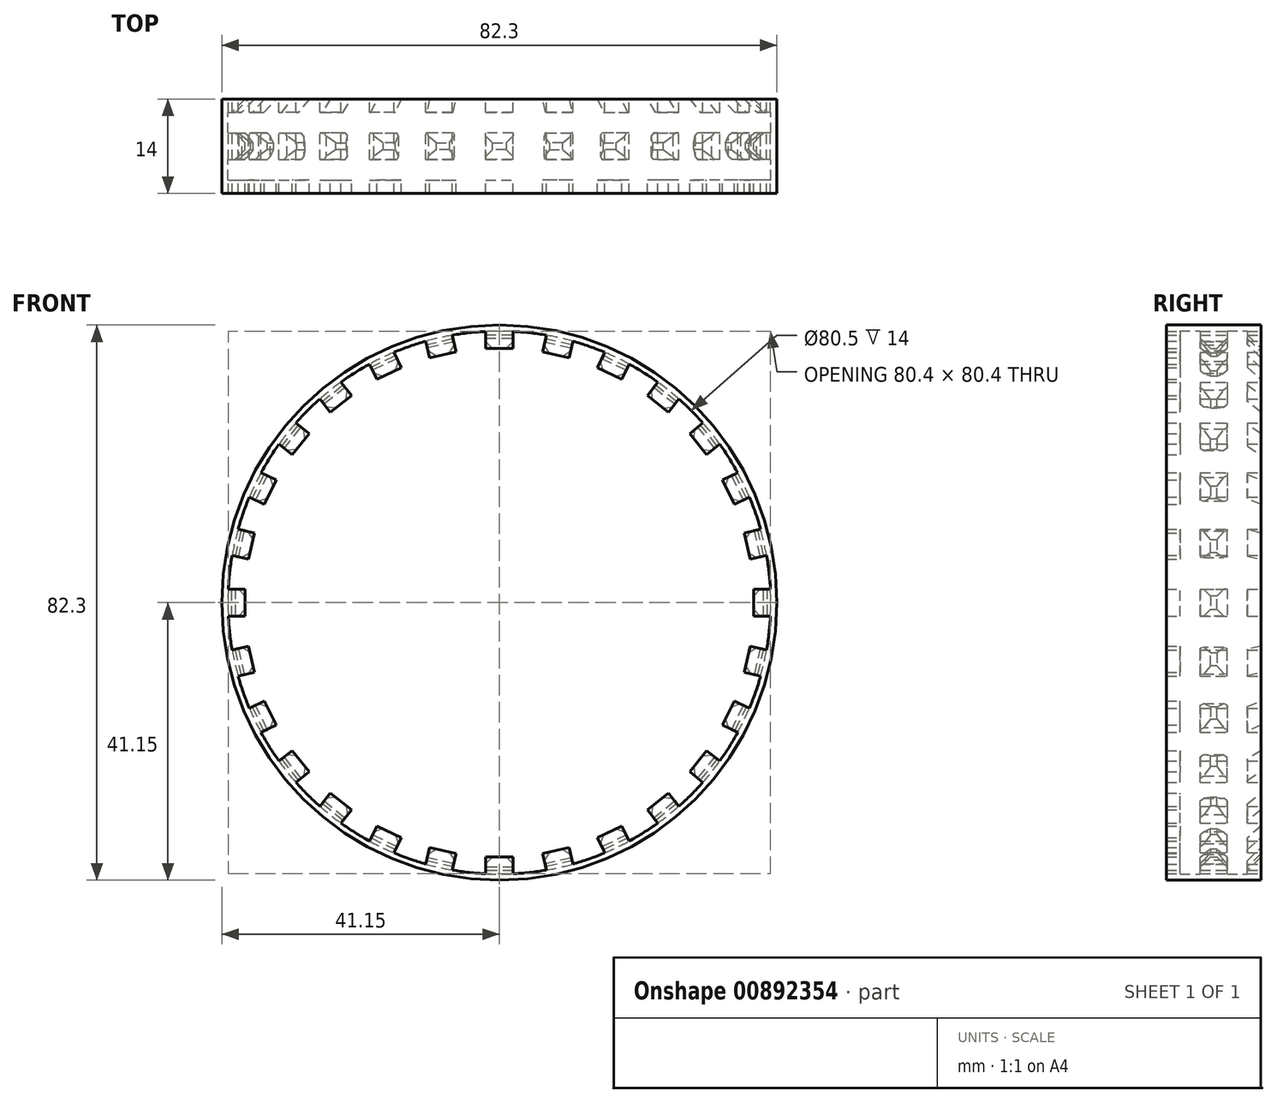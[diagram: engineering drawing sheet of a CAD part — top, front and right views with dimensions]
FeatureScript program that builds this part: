
annotation { "Feature Type Name" : "Feature", "Feature Type Description" : "" }
export const myFeature = defineFeature(function(context is Context, id is Id, definition is map)
    precondition{}
    {
        {
            var Q0;
            Q0=qCreatedBy(makeId("Top.planeOp"),FACE);
            var sketch = newSketch(context, id + "F0", { "sketchPlane" : qUnion([Q0])});
            skLineSegment(sketch, "E0", {"start": v(0, 44.68) * mm, "end": v(0, -51.28) * mm, "construction": true});
            skSolve(sketch);
        }
        {
            var Q0;
            Q0=qCreatedBy(makeId("Front.planeOp"),FACE);
            var sketch = newSketch(context, id + "F1", { "sketchPlane" : qUnion([Q0])});
            skCircle(sketch, "E1", {"center": v(0, 0) * mm, "radius": 40.25 * mm});
            skCircle(sketch, "E2", {"center": v(0, 0) * mm, "radius": 41.15 * mm});
            skLineSegment(sketch, "E3", {"start": v(0, 41.15) * mm, "end": v(0, 40.25) * mm, "construction": true});
            skPoint(sketch, "E4", {"position": v(0, 40.7) * mm});
            skCircle(sketch, "E5", {"center": v(0, 40.7) * mm, "radius": 2 * mm});
            skLineSegment(sketch, "E6.top", {"start": v(-2, 37.7) * mm, "end": v(2, 37.7) * mm});
            skLineSegment(sketch, "E6.left", {"start": v(-2, 40.2) * mm, "end": v(-2, 37.7) * mm});
            skLineSegment(sketch, "E6.right", {"start": v(2, 40.2) * mm, "end": v(2, 37.7) * mm});
            skPoint(sketch, "E7.orphan", {"position": v(2, 40.7) * mm});
            skPoint(sketch, "E8.orphan", {"position": v(-2, 40.7) * mm});
            skSolve(sketch);
        }
        {
            var Q0;
            {var subQ0=sQuery(id+"F1.wireOp",EDGE,"E1");var subQ2=makeQuery(id+"F1.imprint","INTERSECT",VERTEX,{"derivedFrom":[subQ0,sQuery(id+"F1.wireOp",EDGE,"E6.right")]});Q0=makeQuery(id+"F1.imprint","IMPRINT",FACE,{"disambiguationData":[TD([[makeQuery(id+"F1.imprint","IMPRINT",EDGE,{"disambiguationData":[TD([[subQ2,-1.0]])],"derivedFrom":subQ0}),-1.0]])]});}
            var Q1;
            {var subQ0=sQuery(id+"F1.wireOp",EDGE,"E5");var subQ1=sQuery(id+"F1.wireOp",EDGE,"E1");var subQ2=makeQuery(id+"F1.imprint","INTERSECT",VERTEX,{"disambiguationData":[OD(0.0)],"derivedFrom":[subQ1,subQ0]});Q1=makeQuery(id+"F1.imprint","IMPRINT",FACE,{"disambiguationData":[TD([[makeQuery(id+"F1.imprint","IMPRINT",EDGE,{"disambiguationData":[TD([[subQ2,-1.0]])],"derivedFrom":subQ1}),-1.0]])]});}
            extrude(context, id + "F2", {"entities" : qUnion([Q0, Q1]), "endBound" : BoundingType.SYMMETRIC, "depth" : 14 * mm, "offsetDistance" : 25 * mm});
        }
        {
            var Q0;
            {var subQ0=sQuery(id+"F1.wireOp",EDGE,"E5");var subQ1=sQuery(id+"F1.wireOp",EDGE,"E2");var subQ2=makeQuery(id+"F1.imprint","INTERSECT",VERTEX,{"disambiguationData":[OD(0.0)],"derivedFrom":[subQ1,subQ0]});Q0=makeQuery(id+"F1.imprint","IMPRINT",FACE,{"disambiguationData":[TD([[makeQuery(id+"F1.imprint","IMPRINT",EDGE,{"disambiguationData":[TD([[subQ2,1.0]])],"derivedFrom":subQ1}),-1.0]])]});}
            var Q1;
            {var subQ0=sQuery(id+"F1.wireOp",EDGE,"E5");var subQ1=sQuery(id+"F1.wireOp",EDGE,"E1");var subQ2=makeQuery(id+"F1.imprint","INTERSECT",VERTEX,{"disambiguationData":[OD(0.0)],"derivedFrom":[subQ1,subQ0]});Q1=makeQuery(id+"F1.imprint","IMPRINT",FACE,{"disambiguationData":[TD([[makeQuery(id+"F1.imprint","IMPRINT",EDGE,{"disambiguationData":[TD([[subQ2,-1.0]])],"derivedFrom":subQ1}),1.0]])]});}
            var Q2;
            {var subQ0=sQuery(id+"F1.wireOp",EDGE,"E6.right");Q2=makeQuery(id+"F1.imprint","IMPRINT",FACE,{"disambiguationData":[TD([[makeQuery(id+"F1.imprint","IMPRINT",EDGE,{"derivedFrom":subQ0}),-1.0]])]});}
            var Q3;
            {var subQ0=sQuery(id+"F1.wireOp",EDGE,"E6.left");Q3=makeQuery(id+"F1.imprint","IMPRINT",FACE,{"disambiguationData":[TD([[makeQuery(id+"F1.imprint","IMPRINT",EDGE,{"derivedFrom":subQ0}),1.0]])]});}
            var Q4;
            Q4=sQuery(id+"F1.wireOp",EDGE,"E5");
            extrude(context, id + "F3", {"entities" : qUnion([Q0, Q1, Q2, Q3]), "surfaceEntities" : qUnion([Q4]), "endBound" : BoundingType.SYMMETRIC, "depth" : 14 * mm, "offsetDistance" : 25 * mm});
        }
        {
            var Q0;
            {var subQ0=sQuery(id+"F1.wireOp",EDGE,"E5");var subQ1=sQuery(id+"F1.wireOp",EDGE,"E1");var subQ2=makeQuery(id+"F1.imprint","INTERSECT",VERTEX,{"disambiguationData":[OD(0.0)],"derivedFrom":[subQ1,subQ0]});Q0=makeQuery(id+"F1.imprint","IMPRINT",FACE,{"disambiguationData":[TD([[makeQuery(id+"F1.imprint","IMPRINT",EDGE,{"disambiguationData":[TD([[subQ2,1.0]])],"derivedFrom":subQ1}),1.0]])]});}
            var Q1;
            {var subQ0=sQuery(id+"F1.wireOp",EDGE,"E5");var subQ1=sQuery(id+"F1.wireOp",EDGE,"E1");var subQ2=makeQuery(id+"F1.imprint","INTERSECT",VERTEX,{"disambiguationData":[OD(0.0)],"derivedFrom":[subQ1,subQ0]});Q1=makeQuery(id+"F1.imprint","IMPRINT",FACE,{"disambiguationData":[TD([[makeQuery(id+"F1.imprint","IMPRINT",EDGE,{"disambiguationData":[TD([[subQ2,-1.0]])],"derivedFrom":subQ1}),1.0]])]});}
            var Q2;
            {var subQ0=sQuery(id+"F1.wireOp",EDGE,"E6.left");var subQ1=sQuery(id+"F1.wireOp",EDGE,"E1");var subQ2=makeQuery(id+"F1.imprint","INTERSECT",VERTEX,{"derivedFrom":[subQ1,subQ0]});Q2=makeQuery(id+"F1.imprint","IMPRINT",FACE,{"disambiguationData":[TD([[makeQuery(id+"F1.imprint","IMPRINT",EDGE,{"disambiguationData":[TD([[subQ2,1.0]])],"derivedFrom":subQ1}),1.0]])]});}
            var Q3;
            Q3=sQuery(id+"F1.wireOp",EDGE,"E5");
            extrude(context, id + "F4", {"entities" : qUnion([Q0, Q1, Q2]), "operationType" : NewBodyOperationType.REMOVE, "surfaceEntities" : qUnion([Q3]), "endBound" : BoundingType.SYMMETRIC, "oppositeDirection" : true, "depth" : 10 * mm, "offsetDistance" : 25 * mm});
        }
        {
            var Q0;
            Q0=makeQuery(id+"F4.boolean.opBoolean","COPY",EDGE,{"derivedFrom":makeQuery(id+"F4.opExtrude","CAP_EDGE",EDGE,{"disambiguationData":[OSD([sQuery(id+"F1.wireOp",EDGE,"E6.top")])],"isStart":false})});
            var Q1;
            Q1=makeQuery(id+"F4.boolean.opBoolean","COPY",EDGE,{"derivedFrom":makeQuery(id+"F4.opExtrude","CAP_EDGE",EDGE,{"disambiguationData":[OSD([sQuery(id+"F1.wireOp",EDGE,"E6.top")])],"isStart":true})});
            chamfer(context, id + "F5", {"entities" : qUnion([Q0, Q1]), "width" : 2 * mm, "tangentPropagation" : true});
        }
        {
            var Q0;
            {var subQ0=sQuery(id+"F1.wireOp",EDGE,"E5");var subQ1=sQuery(id+"F1.wireOp",EDGE,"E1");var subQ2=makeQuery(id+"F1.imprint","INTERSECT",VERTEX,{"disambiguationData":[OD(0.0)],"derivedFrom":[subQ1,subQ0]});Q0=makeQuery(id+"F1.imprint","IMPRINT",FACE,{"disambiguationData":[TD([[makeQuery(id+"F1.imprint","IMPRINT",EDGE,{"disambiguationData":[TD([[subQ2,1.0]])],"derivedFrom":subQ1}),1.0]])]});}
            var Q1;
            {var subQ0=sQuery(id+"F1.wireOp",EDGE,"E6.left");var subQ1=sQuery(id+"F1.wireOp",EDGE,"E1");var subQ2=makeQuery(id+"F1.imprint","INTERSECT",VERTEX,{"derivedFrom":[subQ1,subQ0]});Q1=makeQuery(id+"F1.imprint","IMPRINT",FACE,{"disambiguationData":[TD([[makeQuery(id+"F1.imprint","IMPRINT",EDGE,{"disambiguationData":[TD([[subQ2,1.0]])],"derivedFrom":subQ1}),1.0]])]});}
            var Q2;
            {var subQ0=sQuery(id+"F1.wireOp",EDGE,"E5");var subQ1=sQuery(id+"F1.wireOp",EDGE,"E1");var subQ2=makeQuery(id+"F1.imprint","INTERSECT",VERTEX,{"disambiguationData":[OD(0.0)],"derivedFrom":[subQ1,subQ0]});Q2=makeQuery(id+"F1.imprint","IMPRINT",FACE,{"disambiguationData":[TD([[makeQuery(id+"F1.imprint","IMPRINT",EDGE,{"disambiguationData":[TD([[subQ2,-1.0]])],"derivedFrom":subQ1}),1.0]])]});}
            extrude(context, id + "F6", {"entities" : qUnion([Q0, Q1, Q2]), "endBound" : BoundingType.SYMMETRIC, "depth" : 4 * mm, "offsetDistance" : 25 * mm});
        }
        {
            var Q0;
            Q0=makeQuery(id+"F6.opExtrude","CAP_EDGE",EDGE,{"disambiguationData":[OSD([sQuery(id+"F1.wireOp",EDGE,"E6.top")])],"isStart":true});
            var Q1;
            Q1=makeQuery(id+"F6.opExtrude","CAP_EDGE",EDGE,{"disambiguationData":[OSD([sQuery(id+"F1.wireOp",EDGE,"E6.top")])],"isStart":false});
            chamfer(context, id + "F7", {"entities" : qUnion([Q0, Q1]), "chamferType" : ChamferType.OFFSET_ANGLE, "width" : 1.5 * mm, "oppositeDirection" : false, "angle" : 45 * degree, "tangentPropagation" : true});
        }
        {
            var Q0;
            Q0=makeQuery(id+"F6.opExtrude","SWEPT_EDGE",EDGE,{"disambiguationData":[OSD([sQuery(id+"F1.wireOp",EDGE,"E6.top"),sQuery(id+"F1.wireOp",EDGE,"E6.left")])]});
            var Q1;
            Q1=makeQuery(id+"F6.opExtrude","SWEPT_EDGE",EDGE,{"disambiguationData":[OSD([sQuery(id+"F1.wireOp",EDGE,"E6.top"),sQuery(id+"F1.wireOp",EDGE,"E6.right")])]});
            chamfer(context, id + "F8", {"entities" : qUnion([Q0, Q1]), "width" : 1 * mm, "tangentPropagation" : true});
        }
        {
            var Q0;
            Q0=makeQuery(id+"F6.opExtrude","SWEPT_BODY",BODY,{"disambiguationData":[OSD([sQuery(id+"F1.wireOp",EDGE,"E1"),sQuery(id+"F1.wireOp",EDGE,"E6.top"),sQuery(id+"F1.wireOp",EDGE,"E6.left"),sQuery(id+"F1.wireOp",EDGE,"E6.right")])]});
            var Q1;
            Q1=makeQuery(id+"F4.boolean.opBoolean","SPLIT",BODY,{"disambiguationData":[OD(1.0)],"derivedFrom":makeQuery(id+"F3.opExtrude","SWEPT_BODY",BODY,{"disambiguationData":[OSD([sQuery(id+"F1.wireOp",EDGE,"E1"),sQuery(id+"F1.wireOp",EDGE,"E6.top"),sQuery(id+"F1.wireOp",EDGE,"E6.left"),sQuery(id+"F1.wireOp",EDGE,"E6.right")])]})});
            var Q2;
            Q2=makeQuery(id+"F4.boolean.opBoolean","SPLIT",BODY,{"disambiguationData":[OD(0.0)],"derivedFrom":makeQuery(id+"F3.opExtrude","SWEPT_BODY",BODY,{"disambiguationData":[OSD([sQuery(id+"F1.wireOp",EDGE,"E1"),sQuery(id+"F1.wireOp",EDGE,"E6.top"),sQuery(id+"F1.wireOp",EDGE,"E6.left"),sQuery(id+"F1.wireOp",EDGE,"E6.right")])]})});
            var Q3;
            Q3=makeQuery(id+"F2.opExtrude","SWEPT_BODY",BODY,{"disambiguationData":[OSD([sQuery(id+"F1.wireOp",EDGE,"E1"),sQuery(id+"F1.wireOp",EDGE,"E2"),sQuery(id+"F1.wireOp",EDGE,"E5")])]});
            var Q4;
            Q4=makeQuery(id+"F3.opExtrude","SWEPT_BODY",BODY,{"disambiguationData":[OSD([sQuery(id+"F1.wireOp",EDGE,"E2"),sQuery(id+"F1.wireOp",EDGE,"E5")])]});
            var Q5;
            Q5=sQuery(id+"F0.wireOp",EDGE,"E0");
            circularPattern(context, id + "F9", {"operationType" : NewBodyOperationType.ADD, "entities" : qUnion([Q0, Q1, Q2, Q3, Q4]), "axis" : qUnion([Q5]), "angle" : 360 * degree, "instanceCount" : 28, "equalSpace" : true});
        }
    });
